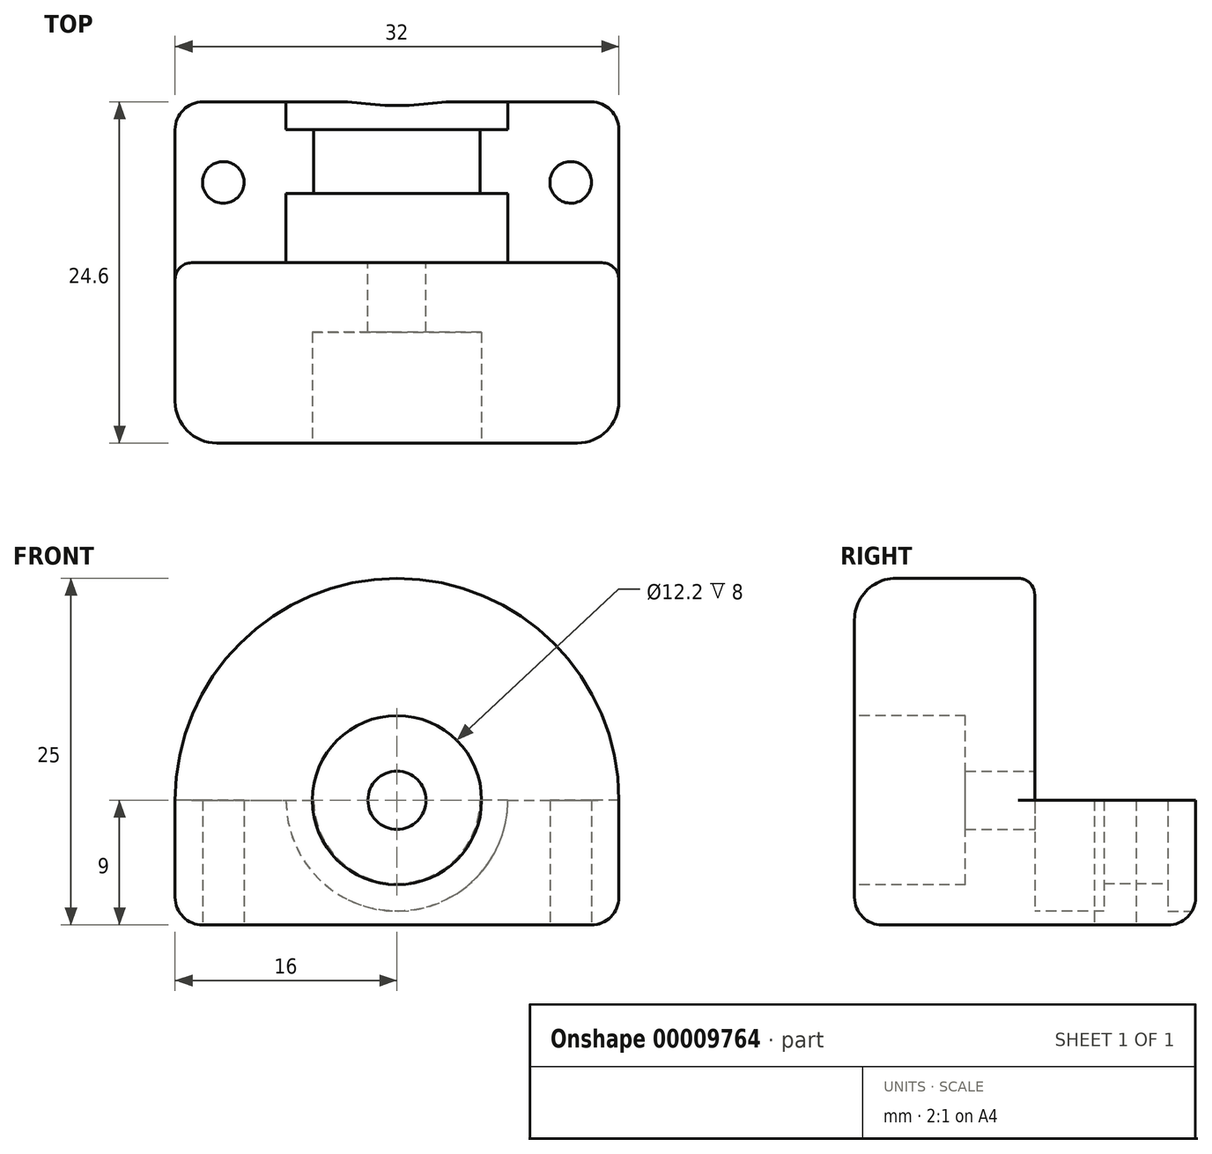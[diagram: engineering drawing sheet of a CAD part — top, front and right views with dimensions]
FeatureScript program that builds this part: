
annotation { "Feature Type Name" : "Feature", "Feature Type Description" : "" }
export const myFeature = defineFeature(function(context is Context, id is Id, definition is map)
    precondition{}
    {
        {
            var Q0;
            Q0=qCreatedBy(makeId("Top.planeOp"),FACE);
            var sketch = newSketch(context, id + "F0", { "sketchPlane" : qUnion([Q0])});
            skLineSegment(sketch, "E0.rect.bottom", {"start": v(-16, 5.8) * mm, "end": v(16, 5.8) * mm});
            skLineSegment(sketch, "E0.rect.top", {"start": v(-16, -5.8) * mm, "end": v(16, -5.8) * mm});
            skLineSegment(sketch, "E0.rect.left", {"start": v(-16, 5.8) * mm, "end": v(-16, -5.8) * mm});
            skLineSegment(sketch, "E0.rect.right", {"start": v(16, 5.8) * mm, "end": v(16, -5.8) * mm});
            skPoint(sketch, "E0.rect.middle", {"position": v(0, 0) * mm});
            skCircle(sketch, "E1", {"center": v(12.52, 0) * mm, "radius": 1.5 * mm});
            skCircle(sketch, "E2", {"center": v(-12.52, 0) * mm, "radius": 1.5 * mm});
            skSolve(sketch);
        }
        {
            var Q0;
            Q0=makeQuery(id+"F0.imprint","IMPRINT",FACE,{"disambiguationData":[TD([[makeQuery(id+"F0.imprint","IMPRINT",EDGE,{"derivedFrom":sQuery(id+"F0.wireOp",EDGE,"E0.rect.bottom")}),-1.0]])]});
            extrude(context, id + "F1", {"entities" : qUnion([Q0]), "depth" : 9 * mm});
        }
        {
            var Q0;
            Q0=makeQuery(id+"F1.opExtrude","SWEPT_FACE",FACE,{"disambiguationData":[OSD([sQuery(id+"F0.wireOp",EDGE,"E0.rect.top")])]});
            var sketch = newSketch(context, id + "F2", { "sketchPlane" : qUnion([Q0])});
            skCircle(sketch, "E3", {"center": v(0, 9) * mm, "radius": 8 * mm});
            skSolve(sketch);
        }
        {
            var Q0;
            Q0=qSketchRegion(id+"F2",true);
            var Q1;
            Q1=makeQuery(id+"F1.opExtrude","SWEPT_FACE",FACE,{"disambiguationData":[OSD([sQuery(id+"F0.wireOp",EDGE,"E0.rect.bottom")])]});
            extrude(context, id + "F3", {"entities" : qUnion([Q0, Q1]), "operationType" : NewBodyOperationType.REMOVE, "oppositeDirection" : true, "depth" : 5 * mm});
        }
        {
            var Q0;
            Q0=makeQuery(id+"F1.opExtrude","SWEPT_FACE",FACE,{"disambiguationData":[OSD([sQuery(id+"F0.wireOp",EDGE,"E0.rect.bottom")])]});
            var sketch = newSketch(context, id + "F4", { "sketchPlane" : qUnion([Q0])});
            skCircle(sketch, "E4", {"center": v(0, 9) * mm, "radius": 8 * mm});
            skSolve(sketch);
        }
        {
            var Q0;
            Q0=qSketchRegion(id+"F4",true);
            extrude(context, id + "F5", {"entities" : qUnion([Q0]), "operationType" : NewBodyOperationType.REMOVE, "oppositeDirection" : true, "depth" : 2 * mm});
        }
        {
            var Q0;
            Q0=makeQuery(id+"F5.boolean.opBoolean","COPY",FACE,{"derivedFrom":makeQuery(id+"F5.opExtrude","CAP_FACE",FACE,{"disambiguationData":[OSD([sQuery(id+"F4.wireOp",EDGE,"E4")])],"isStart":false})});
            var sketch = newSketch(context, id + "F6", { "sketchPlane" : qUnion([Q0])});
            skCircle(sketch, "E5", {"center": v(0, 9) * mm, "radius": 6 * mm});
            skSolve(sketch);
        }
        {
            var Q0;
            Q0=qSketchRegion(id+"F6",true);
            extrude(context, id + "F7", {"entities" : qUnion([Q0]), "operationType" : NewBodyOperationType.REMOVE, "oppositeDirection" : true, "depth" : 25 * mm});
        }
        {
            var Q0;
            Q0=makeQuery(id+"F1.opExtrude","CAP_EDGE",EDGE,{"disambiguationData":[OSD([sQuery(id+"F0.wireOp",EDGE,"E0.rect.bottom")])],"isStart":true});
            var Q1;
            Q1=makeQuery(id+"F7.boolean.opBoolean","COPY",EDGE,{"derivedFrom":makeQuery(id+"F7.opExtrude","CAP_EDGE",EDGE,{"disambiguationData":[OSD([sQuery(id+"F6.wireOp",EDGE,"E5")])],"isStart":true})});
            var Q2;
            Q2=makeQuery(id+"F1.opExtrude","SWEPT_EDGE",EDGE,{"disambiguationData":[OSD([sQuery(id+"F0.wireOp",EDGE,"E0.rect.bottom"),sQuery(id+"F0.wireOp",EDGE,"E0.rect.left")])]});
            var Q3;
            Q3=makeQuery(id+"F1.opExtrude","CAP_EDGE",EDGE,{"disambiguationData":[OSD([sQuery(id+"F0.wireOp",EDGE,"E0.rect.left")])],"isStart":true});
            var Q4;
            Q4=makeQuery(id+"F1.opExtrude","CAP_EDGE",EDGE,{"disambiguationData":[OSD([sQuery(id+"F0.wireOp",EDGE,"E0.rect.right")])],"isStart":true});
            var Q5;
            Q5=makeQuery(id+"F1.opExtrude","SWEPT_EDGE",EDGE,{"disambiguationData":[OSD([sQuery(id+"F0.wireOp",EDGE,"E0.rect.bottom"),sQuery(id+"F0.wireOp",EDGE,"E0.rect.right")])]});
            fillet(context, id + "F8", {"entities" : qUnion([Q0, Q1, Q2, Q3, Q4, Q5]), "radius" : 2 * mm, "tangentPropagation" : true, "allowEdgeOverflow" : false});
        }
        {
            var Q0;
            Q0=makeQuery(id+"F1.opExtrude","SWEPT_FACE",FACE,{"disambiguationData":[OSD([sQuery(id+"F0.wireOp",EDGE,"E0.rect.top")])]});
            var sketch = newSketch(context, id + "F9", { "sketchPlane" : qUnion([Q0])});
            skArc(sketch, "E6", {"start": v(16, 9) * mm, "mid": v(0, 25) * mm, "end": v(-16, 9) * mm});
            skLineSegment(sketch, "E7", {"start": v(0, 0) * mm, "end": v(13.23, 0) * mm});
            skLineSegment(sketch, "E8", {"start": v(-13.23, 0) * mm, "end": v(0, 0) * mm});
            skLineSegment(sketch, "E9", {"start": v(-16, 9) * mm, "end": v(-16, 0) * mm});
            skLineSegment(sketch, "E10", {"start": v(16, 9) * mm, "end": v(16, 0) * mm});
            skLineSegment(sketch, "E11", {"start": v(-16, 0) * mm, "end": v(16, 0) * mm});
            skSolve(sketch);
        }
        {
            var Q0;
            Q0=qSketchRegion(id+"F9",true);
            extrude(context, id + "F10", {"entities" : qUnion([Q0]), "operationType" : NewBodyOperationType.ADD, "depth" : 13 * mm});
        }
        {
            var Q0;
            Q0=makeQuery(id+"F10.opExtrude","CAP_EDGE",EDGE,{"disambiguationData":[OSD([sQuery(id+"F9.wireOp",EDGE,"E6")])],"isStart":false});
            fillet(context, id + "F11", {"entities" : qUnion([Q0]), "radius" : 3 * mm, "tangentPropagation" : true, "allowEdgeOverflow" : false});
        }
        {
            var Q0;
            Q0=makeQuery(id+"F10.opExtrude","CAP_EDGE",EDGE,{"disambiguationData":[OSD([sQuery(id+"F9.wireOp",EDGE,"E6")])],"isStart":true});
            fillet(context, id + "F12", {"entities" : qUnion([Q0]), "radius" : 1.2 * mm, "tangentPropagation" : true, "allowEdgeOverflow" : false});
        }
        {
            var Q0;
            Q0=makeQuery(id+"F10.opExtrude","CAP_FACE",FACE,{"disambiguationData":[OSD([sQuery(id+"F9.wireOp",EDGE,"E6"),sQuery(id+"F9.wireOp",EDGE,"E9"),sQuery(id+"F9.wireOp",EDGE,"E10"),sQuery(id+"F9.wireOp",EDGE,"E11")])],"isStart":false});
            var sketch = newSketch(context, id + "F13", { "sketchPlane" : qUnion([Q0])});
            skCircle(sketch, "E12", {"center": v(0, 9) * mm, "radius": 6.1 * mm});
            skSolve(sketch);
        }
        {
            var Q0;
            Q0=qSketchRegion(id+"F13",true);
            extrude(context, id + "F14", {"entities" : qUnion([Q0]), "operationType" : NewBodyOperationType.REMOVE, "flatOperationType" : FlatOperationType.REMOVE, "oppositeDirection" : true, "depth" : 8 * mm, "offsetDistance" : 25 * mm, "domain" : OperationDomain.MODEL});
        }
        {
            var Q0;
            Q0=makeQuery(id+"F11.opFillet","BLEND_EDGE",EDGE,{"blendedFrom":[makeQuery(id+"F10.opExtrude","CAP_EDGE",EDGE,{"disambiguationData":[OSD([sQuery(id+"F9.wireOp",EDGE,"E9")])],"isStart":false}),makeQuery(id+"F10.boolean.opBoolean","MERGE",FACE,{"derivedFrom":[makeQuery(id+"F1.opExtrude","CAP_FACE",FACE,{"disambiguationData":[OSD([sQuery(id+"F0.wireOp",EDGE,"E0.rect.bottom"),sQuery(id+"F0.wireOp",EDGE,"E0.rect.top"),sQuery(id+"F0.wireOp",EDGE,"E0.rect.left"),sQuery(id+"F0.wireOp",EDGE,"E0.rect.right"),sQuery(id+"F0.wireOp",EDGE,"E1"),sQuery(id+"F0.wireOp",EDGE,"E2")])],"isStart":true}),makeQuery(id+"F10.opExtrude","SWEPT_FACE",FACE,{"disambiguationData":[OSD([sQuery(id+"F9.wireOp",EDGE,"E11")])]})]})],"blendedInto":[makeQuery(id+"F10.boolean.opBoolean","MERGE",FACE,{"derivedFrom":[makeQuery(id+"F1.opExtrude","CAP_FACE",FACE,{"disambiguationData":[OSD([sQuery(id+"F0.wireOp",EDGE,"E0.rect.bottom"),sQuery(id+"F0.wireOp",EDGE,"E0.rect.top"),sQuery(id+"F0.wireOp",EDGE,"E0.rect.left"),sQuery(id+"F0.wireOp",EDGE,"E0.rect.right"),sQuery(id+"F0.wireOp",EDGE,"E1"),sQuery(id+"F0.wireOp",EDGE,"E2")])],"isStart":true}),makeQuery(id+"F10.opExtrude","SWEPT_FACE",FACE,{"disambiguationData":[OSD([sQuery(id+"F9.wireOp",EDGE,"E11")])]})]})]});
            fillet(context, id + "F15", {"entities" : qUnion([Q0]), "radius" : 2 * mm, "tangentPropagation" : true, "allowEdgeOverflow" : false});
        }
        {
            var Q0;
            {var subQ0=sQuery(id+"F9.wireOp",EDGE,"E6");var subQ1=sQuery(id+"F9.wireOp",EDGE,"E9");var subQ2=sQuery(id+"F9.wireOp",EDGE,"E10");Q0=makeQuery(id+"F10.boolean.opBoolean","SPLIT",FACE,{"disambiguationData":[TD([makeQuery(id+"F3.boolean.opBoolean","COPY",FACE,{"derivedFrom":makeQuery(id+"F3.opExtrude","SWEPT_FACE",FACE,{"disambiguationData":[OSD([sQuery(id+"F2.wireOp",EDGE,"E3")])]})})])],"derivedFrom":makeQuery(id+"F10.opExtrude","CAP_FACE",FACE,{"disambiguationData":[OSD([subQ0,subQ1,subQ2,sQuery(id+"F9.wireOp",EDGE,"E11")])],"isStart":true})});}
            var sketch = newSketch(context, id + "F16", { "sketchPlane" : qUnion([Q0])});
            skCircle(sketch, "E13", {"center": v(0, 9) * mm, "radius": 2.1 * mm});
            skSolve(sketch);
        }
        {
            var Q0;
            Q0=qSketchRegion(id+"F16",true);
            extrude(context, id + "F17", {"entities" : qUnion([Q0]), "operationType" : NewBodyOperationType.REMOVE, "oppositeDirection" : true, "depth" : 7 * mm});
        }
    });
